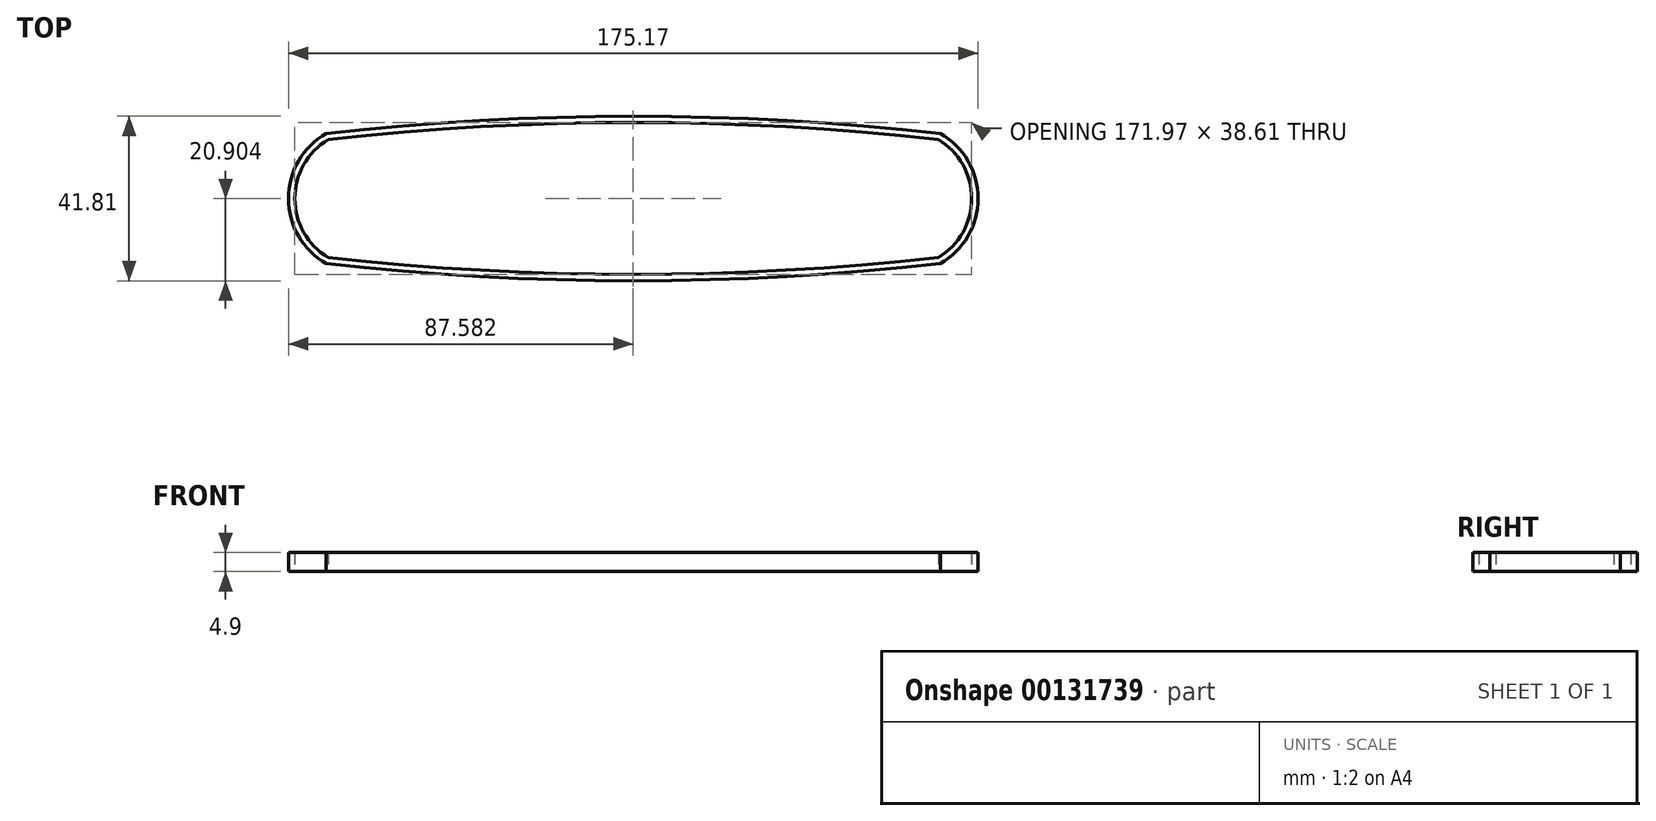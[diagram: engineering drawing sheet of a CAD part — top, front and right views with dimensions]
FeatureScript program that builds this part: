
annotation { "Feature Type Name" : "Feature", "Feature Type Description" : "" }
export const myFeature = defineFeature(function(context is Context, id is Id, definition is map)
    precondition{}
    {
        {
            var Q0;
            Q0=qCreatedBy(makeId("Top.planeOp"),FACE);
            var sketch = newSketch(context, id + "F0", { "sketchPlane" : qUnion([Q0])});
            skLineSegment(sketch, "E0.bottom", {"start": v(-124.99, 9.52) * mm, "end": v(30.01, 9.52) * mm});
            skLineSegment(sketch, "E0.top", {"start": v(-124.99, -20.48) * mm, "end": v(30.01, -20.48) * mm});
            skLineSegment(sketch, "E0.left", {"start": v(-124.99, 9.52) * mm, "end": v(-124.99, -20.48) * mm});
            skLineSegment(sketch, "E0.right", {"start": v(30.01, 9.52) * mm, "end": v(30.01, -20.48) * mm});
            skPoint(sketch, "E1.end.orphan", {"position": v(-124.99, -23.8) * mm});
            skArc(sketch, "E2", {"start": v(-124.99, 9.52) * mm, "mid": v(-133.47, -5.48) * mm, "end": v(-124.99, -20.48) * mm});
            skArc(sketch, "E3", {"start": v(30.01, -20.48) * mm, "mid": v(38.5, -5.48) * mm, "end": v(30.01, 9.52) * mm});
            skArc(sketch, "E4", {"start": v(30.01, 9.52) * mm, "mid": v(-47.49, 13.83) * mm, "end": v(-124.99, 9.52) * mm});
            skArc(sketch, "E5", {"start": v(-124.99, -20.48) * mm, "mid": v(-47.49, -24.78) * mm, "end": v(30.01, -20.48) * mm});
            skArc(sketch, "E6.0", {"start": v(30.53, 11.08) * mm, "mid": v(-47.49, 15.43) * mm, "end": v(-125.5, 11.08) * mm});
            skArc(sketch, "E6.1", {"start": v(30.53, -22.03) * mm, "mid": v(40.1, -5.48) * mm, "end": v(30.53, 11.08) * mm});
            skArc(sketch, "E6.2", {"start": v(-125.5, -22.03) * mm, "mid": v(-47.49, -26.38) * mm, "end": v(30.53, -22.03) * mm});
            skArc(sketch, "E6.3", {"start": v(-125.5, 11.08) * mm, "mid": v(-135.07, -5.48) * mm, "end": v(-125.5, -22.03) * mm});
            skSolve(sketch);
        }
        {
            var Q0;
            Q0=makeQuery(id+"F0.imprint","IMPRINT",FACE,{"disambiguationData":[TD([[makeQuery(id+"F0.imprint","IMPRINT",EDGE,{"derivedFrom":sQuery(id+"F0.wireOp",EDGE,"E2")}),-1.0]])]});
            extrude(context, id + "F1", {"entities" : qUnion([Q0]), "depth" : 4.9 * mm});
        }
    });
